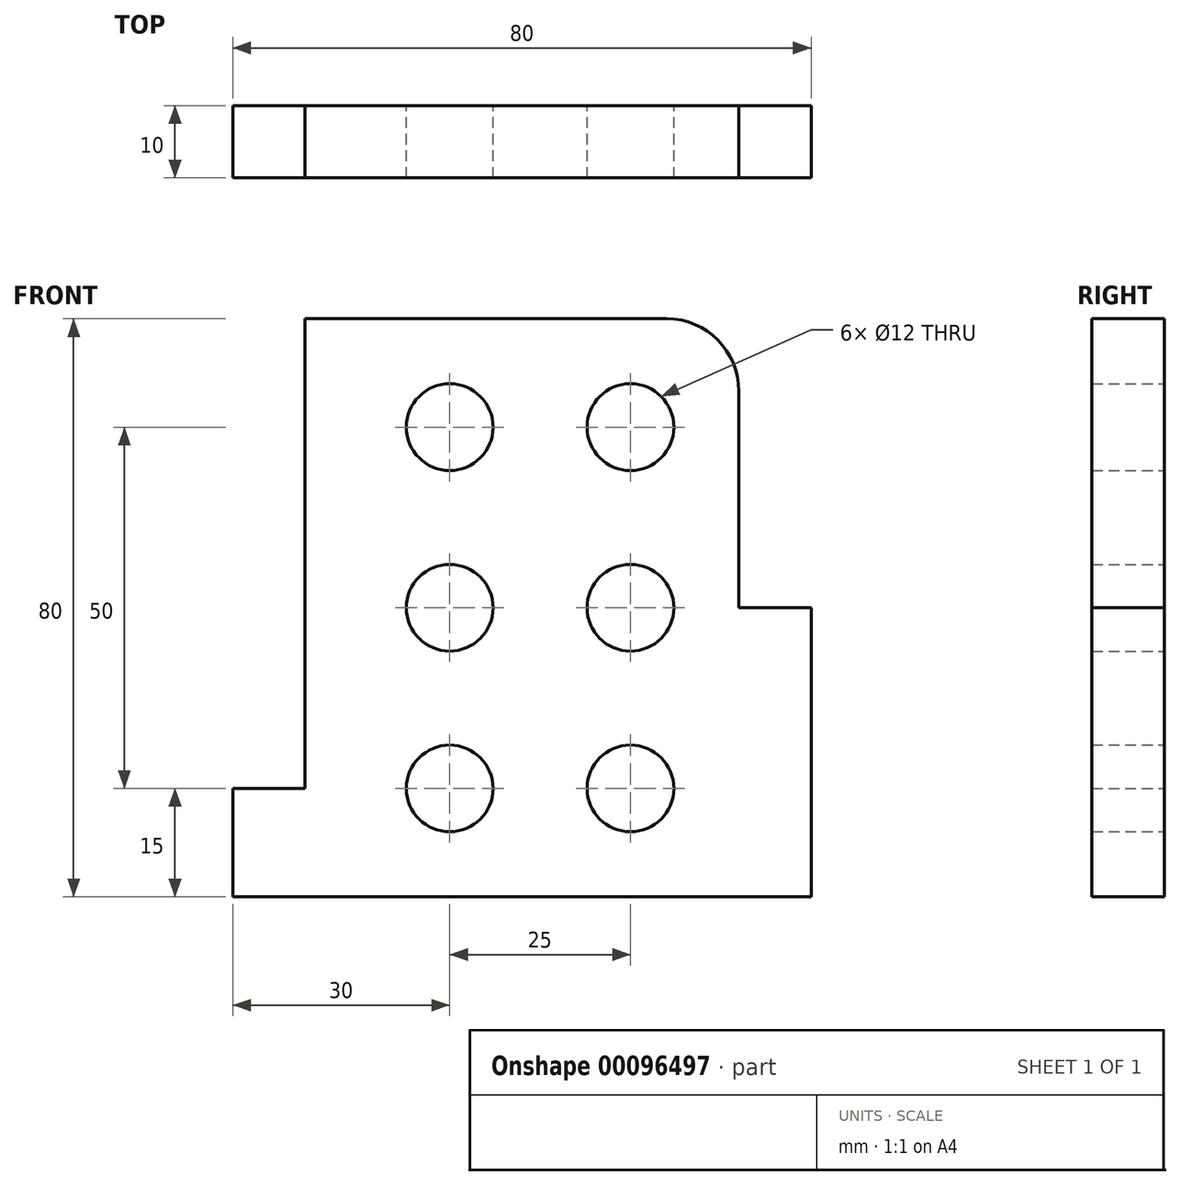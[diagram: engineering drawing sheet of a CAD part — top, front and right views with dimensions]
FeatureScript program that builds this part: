
annotation { "Feature Type Name" : "Feature", "Feature Type Description" : "" }
export const myFeature = defineFeature(function(context is Context, id is Id, definition is map)
    precondition{}
    {
        {
            var Q0;
            Q0=qCreatedBy(makeId("Front.planeOp"),FACE);
            var sketch = newSketch(context, id + "F0", { "sketchPlane" : qUnion([Q0])});
            skLineSegment(sketch, "E0", {"start": v(0, 0) * mm, "end": v(80, 0) * mm});
            skLineSegment(sketch, "E1", {"start": v(80, 0) * mm, "end": v(80, 40) * mm});
            skLineSegment(sketch, "E2", {"start": v(80, 40) * mm, "end": v(70, 40) * mm});
            skLineSegment(sketch, "E3", {"start": v(70, 40) * mm, "end": v(70, 70) * mm});
            skLineSegment(sketch, "E4", {"start": v(60, 80) * mm, "end": v(10, 80) * mm});
            skLineSegment(sketch, "E5", {"start": v(10, 80) * mm, "end": v(10, 15) * mm});
            skLineSegment(sketch, "E6", {"start": v(10, 15) * mm, "end": v(0, 15) * mm});
            skLineSegment(sketch, "E7", {"start": v(0, 15) * mm, "end": v(0, 0) * mm});
            skCircle(sketch, "E8", {"center": v(30, 15) * mm, "radius": 6 * mm});
            skCircle(sketch, "E9", {"center": v(55, 15) * mm, "radius": 6 * mm});
            skCircle(sketch, "E10", {"center": v(30, 40) * mm, "radius": 6 * mm});
            skCircle(sketch, "E11", {"center": v(55, 40) * mm, "radius": 6 * mm});
            skCircle(sketch, "E12", {"center": v(30, 65) * mm, "radius": 6 * mm});
            skCircle(sketch, "E13", {"center": v(55, 65) * mm, "radius": 6 * mm});
            skPoint(sketch, "E14.visualSharp", {"position": v(70, 80) * mm});
            skArc(sketch, "E14.filletArc", {"start": v(70, 70) * mm, "mid": v(67.07, 77.07) * mm, "end": v(60, 80) * mm});
            skSolve(sketch);
        }
        {
            var Q0;
            Q0=makeQuery(id+"F0.imprint","IMPRINT",FACE,{"disambiguationData":[TD([[makeQuery(id+"F0.imprint","IMPRINT",EDGE,{"derivedFrom":sQuery(id+"F0.wireOp",EDGE,"E0")}),1.0]])]});
            extrude(context, id + "F1", {"entities" : qUnion([Q0]), "depth" : 10 * mm});
        }
    });
